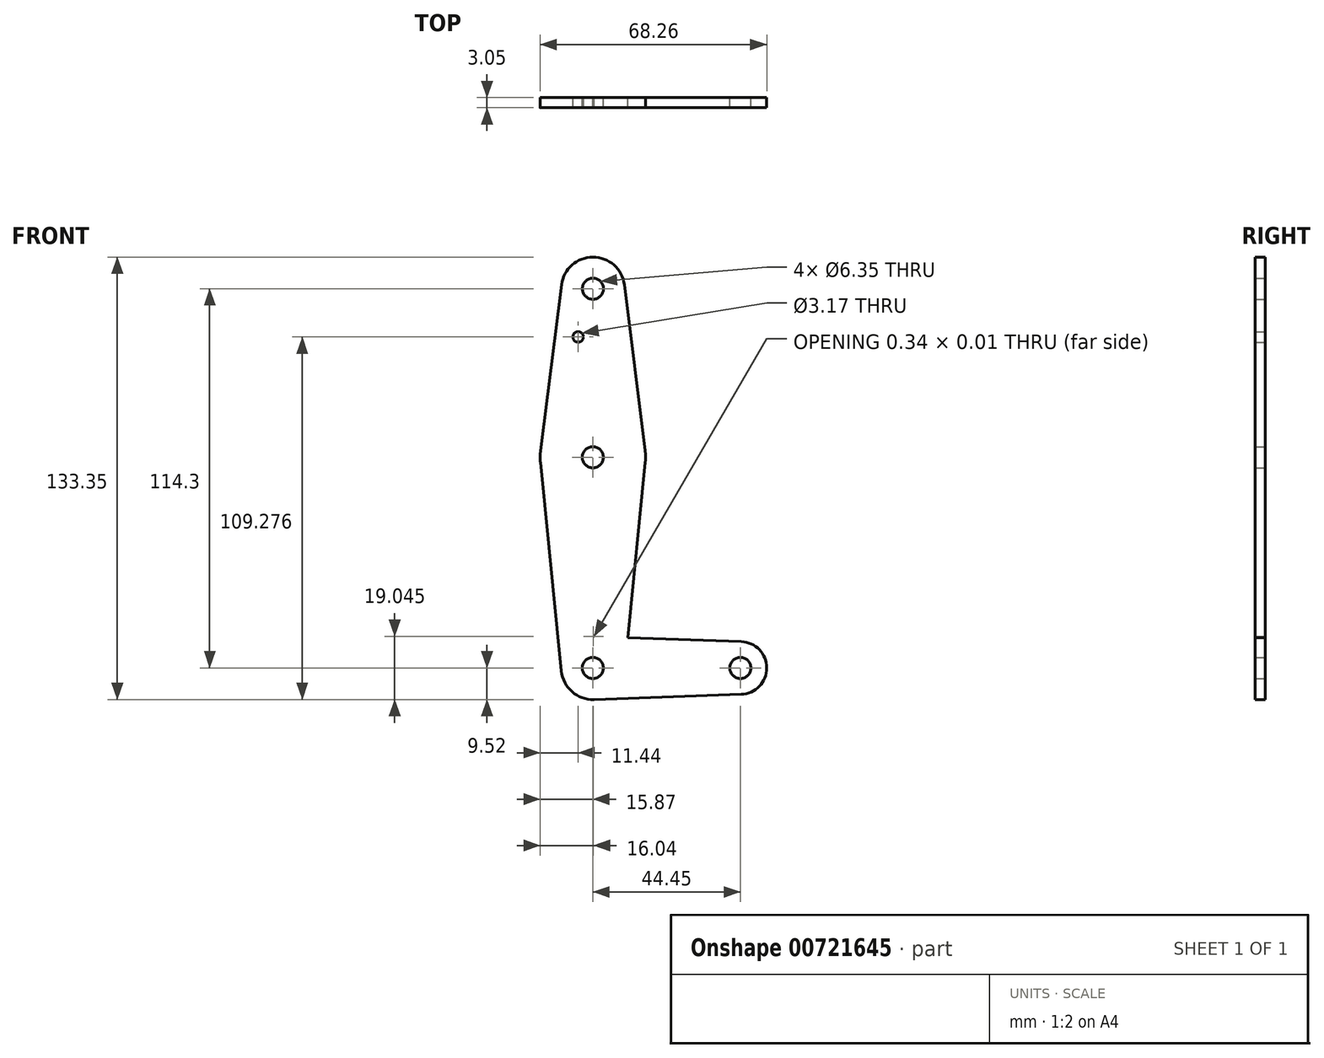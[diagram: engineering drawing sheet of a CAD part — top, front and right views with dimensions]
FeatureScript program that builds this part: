
annotation { "Feature Type Name" : "Feature", "Feature Type Description" : "" }
export const myFeature = defineFeature(function(context is Context, id is Id, definition is map)
    precondition{}
    {
        {
            var Q0;
            Q0=qCreatedBy(makeId("Front.planeOp"),FACE);
            var sketch = newSketch(context, id + "F0", { "sketchPlane" : qUnion([Q0])});
            skCircle(sketch, "E0", {"center": v(0, 0) * mm, "radius": 9.53 * mm});
            skLineSegment(sketch, "E1", {"start": v(0, 0) * mm, "end": v(44.45, 0) * mm});
            skCircle(sketch, "E2", {"center": v(44.45, 0) * mm, "radius": 7.94 * mm});
            skCircle(sketch, "E3", {"center": v(0.03, 114.3) * mm, "radius": 9.53 * mm});
            skCircle(sketch, "E4", {"center": v(0, 63.5) * mm, "radius": 15.88 * mm});
            skLineSegment(sketch, "E5", {"start": v(0, 63.5) * mm, "end": v(0, 0) * mm});
            skLineSegment(sketch, "E6", {"start": v(0, 63.5) * mm, "end": v(0.03, 114.3) * mm});
            skLineSegment(sketch, "E7", {"start": v(0.34, -9.52) * mm, "end": v(44.73, -7.93) * mm});
            skLineSegment(sketch, "E8", {"start": v(44.73, 7.93) * mm, "end": v(0, 9.53) * mm});
            skLineSegment(sketch, "E9", {"start": v(15.75, 65.48) * mm, "end": v(9.48, 115.49) * mm});
            skLineSegment(sketch, "E10", {"start": v(15.8, 61.91) * mm, "end": v(9.57, 0) * mm});
            skLineSegment(sketch, "E11", {"start": v(-9.42, 115.5) * mm, "end": v(-15.75, 65.5) * mm});
            skCircle(sketch, "E12", {"center": v(0, 63.5) * mm, "radius": 3.18 * mm});
            skCircle(sketch, "E13", {"center": v(0.03, 114.3) * mm, "radius": 3.18 * mm});
            skCircle(sketch, "E14", {"center": v(44.45, 0) * mm, "radius": 3.18 * mm});
            skCircle(sketch, "E15", {"center": v(0, 0) * mm, "radius": 3.18 * mm});
            skCircle(sketch, "E16", {"center": v(-4.43, 99.76) * mm, "radius": 1.59 * mm});
            skArc(sketch, "E17", {"start": v(11.34, 17.6) * mm, "mid": v(13.26, 11.57) * mm, "end": v(18.97, 8.85) * mm});
            skLineSegment(sketch, "E18", {"start": v(-15.8, 61.91) * mm, "end": v(-9.48, -0.95) * mm});
            skSolve(sketch);
        }
        {
            var Q0;
            Q0=makeQuery(id+"F0.imprint","IMPRINT",FACE,{"disambiguationData":[TD([[makeQuery(id+"F0.imprint","IMPRINT",EDGE,{"derivedFrom":sQuery(id+"F0.wireOp",EDGE,"E13")}),-1.0]])]});
            var Q1;
            {var subQ0=sQuery(id+"F0.wireOp",EDGE,"E11");Q1=makeQuery(id+"F0.imprint","IMPRINT",FACE,{"disambiguationData":[TD([[makeQuery(id+"F0.imprint","IMPRINT",EDGE,{"derivedFrom":subQ0}),1.0]])]});}
            var Q2;
            {var subQ0=sQuery(id+"F0.wireOp",EDGE,"E9");Q2=makeQuery(id+"F0.imprint","IMPRINT",FACE,{"disambiguationData":[TD([[makeQuery(id+"F0.imprint","IMPRINT",EDGE,{"derivedFrom":subQ0}),1.0]])]});}
            var Q3;
            {var subQ1=sQuery(id+"F0.wireOp",EDGE,"E4");var subQ8=makeQuery(id+"F0.imprint","INTERSECT",VERTEX,{"derivedFrom":[subQ1,sQuery(id+"F0.wireOp",EDGE,"E9")]});Q3=makeQuery(id+"F0.imprint","IMPRINT",FACE,{"disambiguationData":[TD([[makeQuery(id+"F0.imprint","IMPRINT",EDGE,{"disambiguationData":[TD([[subQ8,-1.0]])],"derivedFrom":subQ1}),1.0]])]});}
            var Q4;
            {var subQ4=sQuery(id+"F0.wireOp",EDGE,"E18");Q4=makeQuery(id+"F0.imprint","IMPRINT",FACE,{"disambiguationData":[TD([[makeQuery(id+"F0.imprint","IMPRINT",EDGE,{"derivedFrom":subQ4}),1.0]])]});}
            var Q5;
            {var subQ2=sQuery(id+"F0.wireOp",EDGE,"E10");var subQ6=sQuery(id+"F0.wireOp",EDGE,"E4");var subQ8=makeQuery(id+"F0.imprint","INTERSECT",VERTEX,{"derivedFrom":[subQ6,subQ2]});Q5=makeQuery(id+"F0.imprint","IMPRINT",FACE,{"disambiguationData":[TD([[makeQuery(id+"F0.imprint","IMPRINT",EDGE,{"disambiguationData":[TD([[subQ8,1.0]])],"derivedFrom":subQ6}),-1.0]])]});}
            var Q6;
            {var subQ1=sQuery(id+"F0.wireOp",EDGE,"E0");var subQ6=makeQuery(id+"F0.imprint","INTERSECT",VERTEX,{"derivedFrom":[subQ1,sQuery(id+"F0.wireOp",EDGE,"E18")]});Q6=makeQuery(id+"F0.imprint","IMPRINT",FACE,{"disambiguationData":[TD([[makeQuery(id+"F0.imprint","IMPRINT",EDGE,{"disambiguationData":[TD([[subQ6,1.0]])],"derivedFrom":subQ1}),1.0]])]});}
            var Q7;
            {var subQ2=sQuery(id+"F0.wireOp",EDGE,"E10");var subQ6=sQuery(id+"F0.wireOp",EDGE,"E1");var subQ8=makeQuery(id+"F0.imprint","INTERSECT",VERTEX,{"derivedFrom":[subQ6,subQ2]});Q7=makeQuery(id+"F0.imprint","IMPRINT",FACE,{"disambiguationData":[TD([[makeQuery(id+"F0.imprint","IMPRINT",EDGE,{"disambiguationData":[TD([[subQ8,-1.0]])],"derivedFrom":subQ6}),1.0]])]});}
            var Q8;
            {var subQ0=sQuery(id+"F0.wireOp",EDGE,"E7");Q8=makeQuery(id+"F0.imprint","IMPRINT",FACE,{"disambiguationData":[TD([[makeQuery(id+"F0.imprint","IMPRINT",EDGE,{"derivedFrom":subQ0}),1.0]])]});}
            var Q9;
            {var subQ1=sQuery(id+"F0.wireOp",EDGE,"E0");var subQ5=makeQuery(id+"F0.imprint","INTERSECT",VERTEX,{"derivedFrom":[subQ1,sQuery(id+"F0.wireOp",EDGE,"E8")]});Q9=makeQuery(id+"F0.imprint","IMPRINT",FACE,{"disambiguationData":[TD([[makeQuery(id+"F0.imprint","IMPRINT",EDGE,{"disambiguationData":[TD([[subQ5,1.0]])],"derivedFrom":subQ1}),1.0]])]});}
            var Q10;
            {var subQ0=sQuery(id+"F0.wireOp",EDGE,"E8");var subQ1=sQuery(id+"F0.wireOp",EDGE,"E0");var subQ2=makeQuery(id+"F0.imprint","INTERSECT",VERTEX,{"derivedFrom":[subQ1,subQ0]});Q10=makeQuery(id+"F0.imprint","IMPRINT",FACE,{"disambiguationData":[TD([[makeQuery(id+"F0.imprint","IMPRINT",EDGE,{"disambiguationData":[TD([[subQ2,1.0]])],"derivedFrom":subQ1}),-1.0]])]});}
            var Q11;
            Q11=makeQuery(id+"F0.imprint","IMPRINT",FACE,{"disambiguationData":[TD([[makeQuery(id+"F0.imprint","IMPRINT",EDGE,{"derivedFrom":sQuery(id+"F0.wireOp",EDGE,"E14")}),-1.0]])]});
            var Q12;
            {var subQ0=sQuery(id+"F0.wireOp",EDGE,"E4");var subQ8=makeQuery(id+"F0.imprint","INTERSECT",VERTEX,{"derivedFrom":[subQ0,sQuery(id+"F0.wireOp",EDGE,"E11")]});Q12=makeQuery(id+"F0.imprint","IMPRINT",FACE,{"disambiguationData":[TD([[makeQuery(id+"F0.imprint","IMPRINT",EDGE,{"disambiguationData":[TD([[subQ8,1.0]])],"derivedFrom":subQ0}),1.0]])]});}
            extrude(context, id + "F1", {"entities" : qUnion([Q0, Q1, Q2, Q3, Q4, Q5, Q6, Q7, Q8, Q9, Q10, Q11, Q12]), "depth" : 3.05 * mm, "offsetDistance" : 25.4 * mm});
        }
    });
